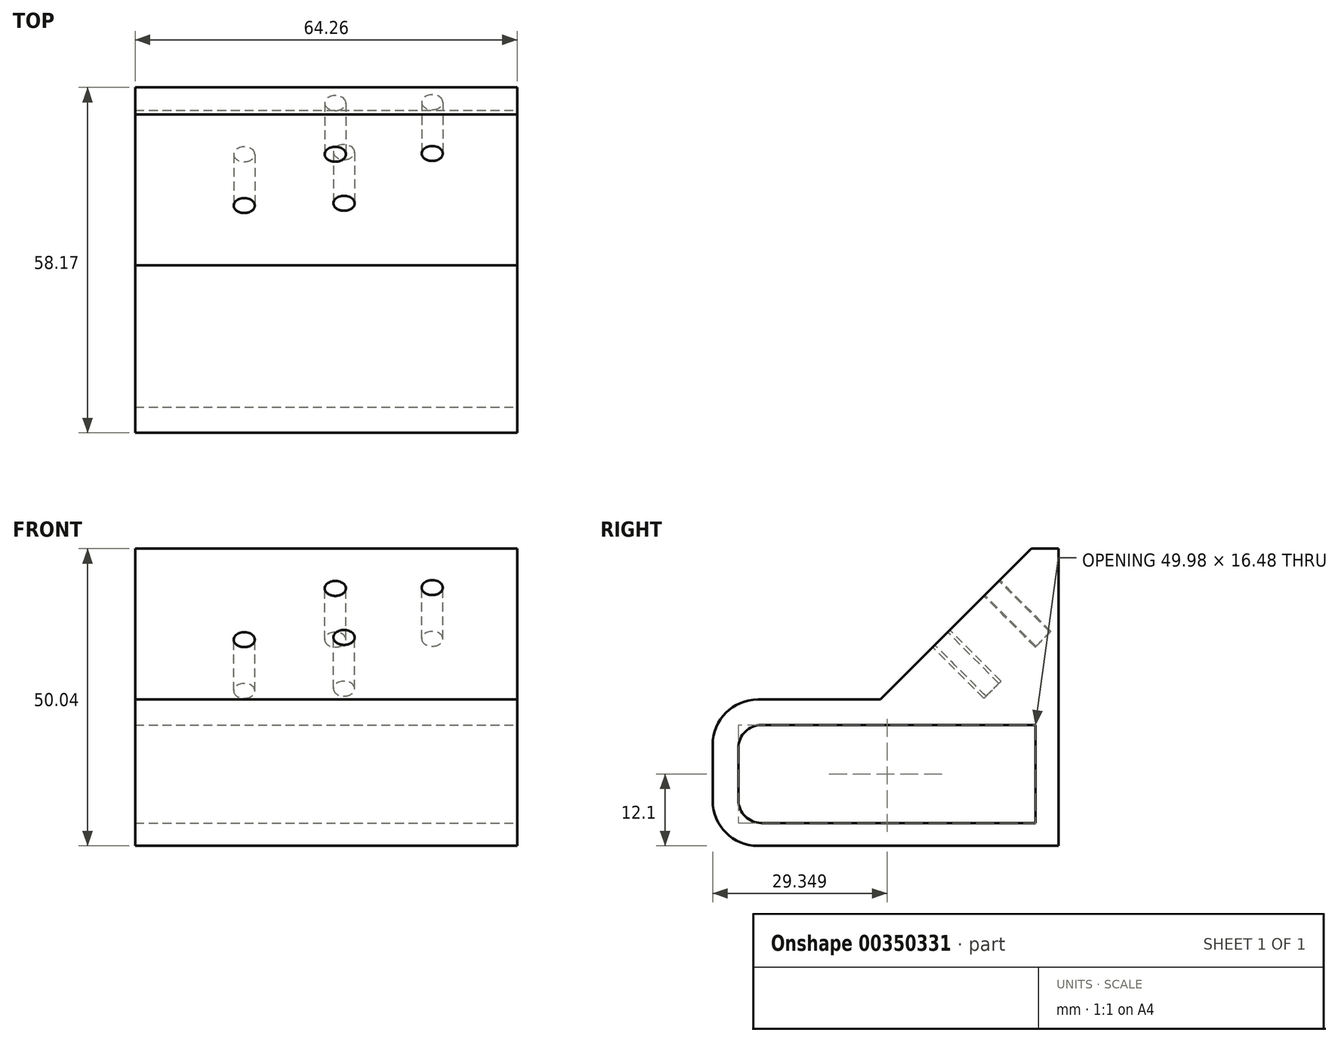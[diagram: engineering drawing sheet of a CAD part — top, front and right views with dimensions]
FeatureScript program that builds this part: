
annotation { "Feature Type Name" : "Feature", "Feature Type Description" : "" }
export const myFeature = defineFeature(function(context is Context, id is Id, definition is map)
    precondition{}
    {
        {
            var Q0;
            Q0=qCreatedBy(makeId("Right.planeOp"),FACE);
            var sketch = newSketch(context, id + "F0", { "sketchPlane" : qUnion([Q0])});
            skLineSegment(sketch, "E0.bottom", {"start": v(-27.67, 16.35) * mm, "end": v(2.3, 16.35) * mm});
            skLineSegment(sketch, "E0.top", {"start": v(-27.67, -33.69) * mm, "end": v(2.3, -33.69) * mm});
            skLineSegment(sketch, "E0.left", {"start": v(-27.67, 16.35) * mm, "end": v(-27.67, -33.69) * mm});
            skLineSegment(sketch, "E0.right", {"start": v(2.3, 16.35) * mm, "end": v(2.3, -33.69) * mm});
            skSolve(sketch);
        }
        {
            var Q0;
            Q0 = qSketchRegion(id + "F0", true);
            extrude(context, id + "F1", {"entities" : qUnion([Q0]), "depth" : 64.26 * mm});
        }
        {
            var Q0;
            Q0=makeQuery(id+"F1.opExtrude","SWEPT_EDGE",EDGE,{"disambiguationData":[OSD([sQuery(id+"F0.wireOp",EDGE,"E0.bottom"),sQuery(id+"F0.wireOp",EDGE,"E0.left")])]});
            chamfer(context, id + "F2", {"entities" : qUnion([Q0]), "width" : 25.4 * mm, "tangentPropagation" : true});
        }
        {
            var Q0;
            Q0=makeQuery(id+"F1.opExtrude","SWEPT_FACE",FACE,{"disambiguationData":[OSD([sQuery(id+"F0.wireOp",EDGE,"E0.left")])]});
            extrude(context, id + "F3", {"entities" : qUnion([Q0]), "operationType" : NewBodyOperationType.ADD, "depth" : 28.2 * mm});
        }
        {
            var Q0;
            Q0=makeQuery(id+"F3.opExtrude","CAP_EDGE",EDGE,{"disambiguationData":[OSD([sQuery(id+"F0.wireOp",EDGE,"E0.bottom"),sQuery(id+"F0.wireOp",EDGE,"E0.left")])],"isStart":false});
            var Q1;
            Q1=makeQuery(id+"F3.opExtrude","CAP_EDGE",EDGE,{"disambiguationData":[OSD([sQuery(id+"F0.wireOp",EDGE,"E0.top"),sQuery(id+"F0.wireOp",EDGE,"E0.left")])],"isStart":false});
            fillet(context, id + "F4", {"entities" : qUnion([Q0, Q1]), "radius" : 7.62 * mm, "tangentPropagation" : true, "allowEdgeOverflow" : false});
        }
        {
            var Q0;
            Q0=makeQuery(id+"F2.opChamfer","BLEND_FACE",FACE,{"disambiguationData":[OSD([sQuery(id+"F0.wireOp",EDGE,"E0.bottom"),sQuery(id+"F0.wireOp",EDGE,"E0.left")])]});
            var sketch = newSketch(context, id + "F5", { "sketchPlane" : qUnion([Q0])});
            skCircle(sketch, "E1", {"center": v(35.14, -11.19) * mm, "radius": 1.78 * mm});
            skCircle(sketch, "E2", {"center": v(49.97, 0.68) * mm, "radius": 1.78 * mm});
            skCircle(sketch, "E3", {"center": v(33.67, 0.49) * mm, "radius": 1.78 * mm});
            skCircle(sketch, "E4", {"center": v(18.35, -11.71) * mm, "radius": 1.78 * mm});
            skSolve(sketch);
        }
        {
            var Q0;
            Q0 = qSketchRegion(id + "F5", true);
            extrude(context, id + "F6", {"entities" : qUnion([Q0]), "operationType" : NewBodyOperationType.REMOVE, "oppositeDirection" : true, "depth" : 12.2 * mm});
        }
        {
            var Q0;
            {var subQ0=sQuery(id+"F0.wireOp",EDGE,"E0.left");Q0=makeQuery(id+"F3.boolean.opBoolean","MERGE",FACE,{"derivedFrom":[makeQuery(id+"F1.opExtrude","CAP_FACE",FACE,{"disambiguationData":[OSD([sQuery(id+"F0.wireOp",EDGE,"E0.bottom"),sQuery(id+"F0.wireOp",EDGE,"E0.top"),subQ0,sQuery(id+"F0.wireOp",EDGE,"E0.right")])],"isStart":false}),makeQuery(id+"F3.opExtrude","SWEPT_FACE",FACE,{"disambiguationData":[OSD([subQ0]),TDD([makeQuery(id+"F1.opExtrude","CAP_EDGE",EDGE,{"disambiguationData":[OSD([subQ0])],"isStart":false})])]})]});}
            var sketch = newSketch(context, id + "F7", { "sketchPlane" : qUnion([Q0])});
            skLineSegment(sketch, "E5.bottom", {"start": v(-1.53, -29.83) * mm, "end": v(-51.51, -29.83) * mm});
            skLineSegment(sketch, "E5.top", {"start": v(-1.53, -13.35) * mm, "end": v(-51.51, -13.35) * mm});
            skLineSegment(sketch, "E5.left", {"start": v(-1.53, -29.83) * mm, "end": v(-1.53, -13.35) * mm});
            skLineSegment(sketch, "E5.right", {"start": v(-51.51, -29.83) * mm, "end": v(-51.51, -13.35) * mm});
            skSolve(sketch);
        }
        {
            var Q0;
            Q0 = qSketchRegion(id + "F7", true);
            extrude(context, id + "F8", {"entities" : qUnion([Q0]), "operationType" : NewBodyOperationType.REMOVE, "oppositeDirection" : true, "depth" : 137.16 * mm});
        }
        {
            var Q0;
            Q0=makeQuery(id+"F8.boolean.opBoolean","COPY",EDGE,{"derivedFrom":makeQuery(id+"F8.opExtrude","SWEPT_EDGE",EDGE,{"disambiguationData":[OSD([sQuery(id+"F7.wireOp",EDGE,"E5.top"),sQuery(id+"F7.wireOp",EDGE,"E5.right")])]})});
            var Q1;
            Q1=makeQuery(id+"F8.boolean.opBoolean","COPY",EDGE,{"derivedFrom":makeQuery(id+"F8.opExtrude","SWEPT_EDGE",EDGE,{"disambiguationData":[OSD([sQuery(id+"F7.wireOp",EDGE,"E5.bottom"),sQuery(id+"F7.wireOp",EDGE,"E5.right")])]})});
            fillet(context, id + "F9", {"entities" : qUnion([Q0, Q1]), "radius" : 3.8 * mm, "tangentPropagation" : true, "allowEdgeOverflow" : false});
        }
    });
